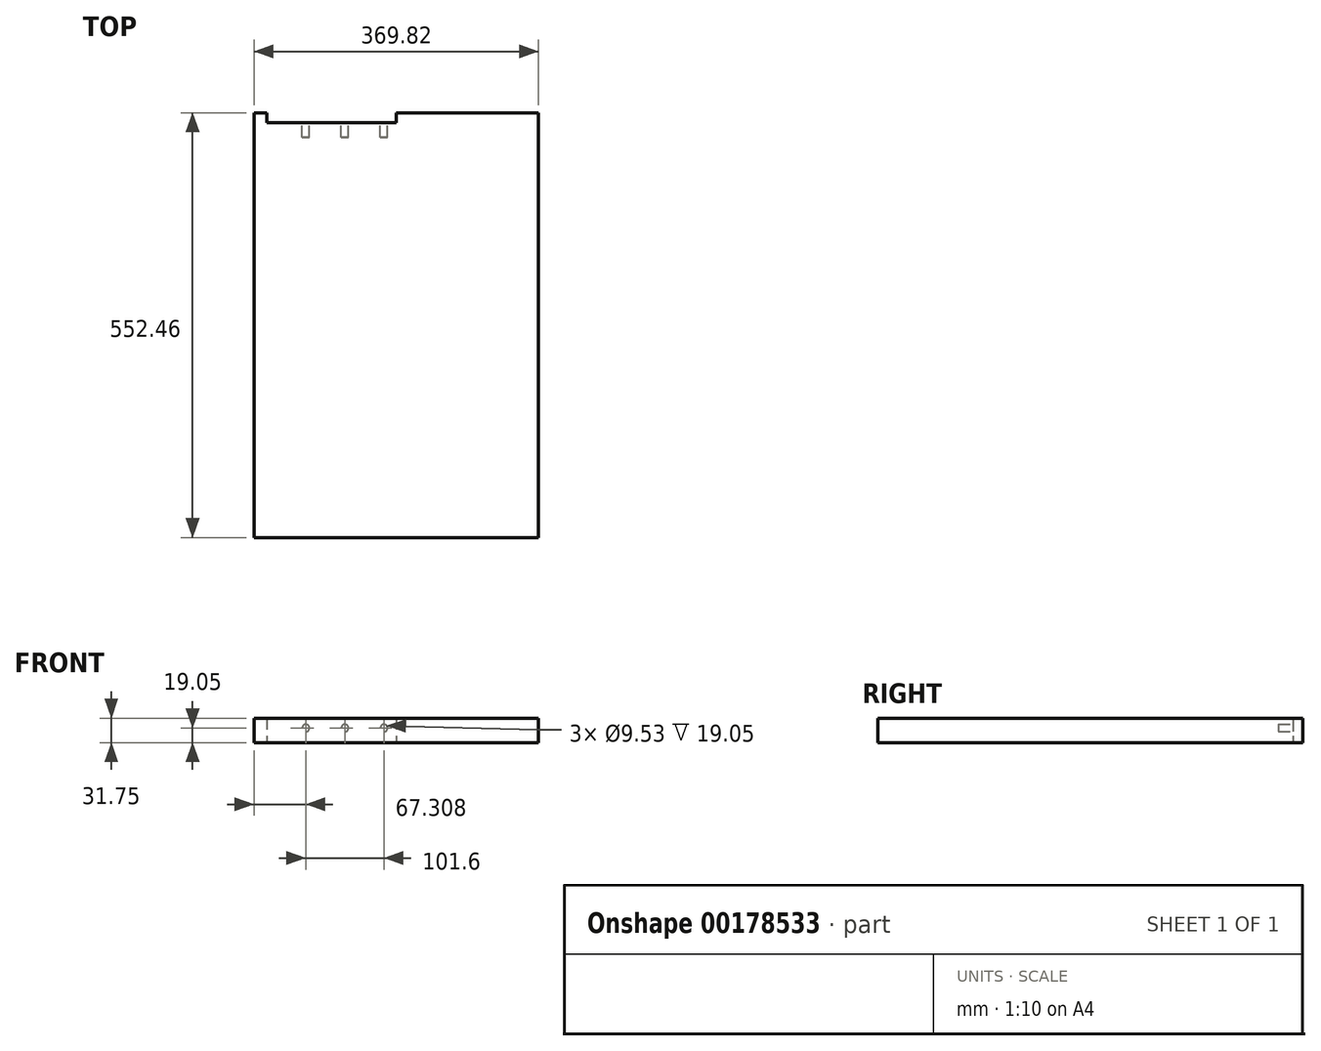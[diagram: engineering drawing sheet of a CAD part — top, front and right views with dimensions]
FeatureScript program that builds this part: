
annotation { "Feature Type Name" : "Feature", "Feature Type Description" : "" }
export const myFeature = defineFeature(function(context is Context, id is Id, definition is map)
    precondition{}
    {
        {
            var Q0;
            Q0=qCreatedBy(makeId("Top.planeOp"),FACE);
            var sketch = newSketch(context, id + "F0", { "sketchPlane" : qUnion([Q0])});
            skLineSegment(sketch, "E0.bottom", {"start": v(184.91, 276.23) * mm, "end": v(-0.13, 276.23) * mm});
            skLineSegment(sketch, "E0.top", {"start": v(184.91, -276.23) * mm, "end": v(-184.91, -276.23) * mm});
            skLineSegment(sketch, "E0.left", {"start": v(184.91, 276.23) * mm, "end": v(184.91, -276.23) * mm});
            skLineSegment(sketch, "E0.right", {"start": v(-184.91, 276.23) * mm, "end": v(-184.91, -276.23) * mm});
            skPoint(sketch, "E0.middle", {"position": v(0, 0) * mm});
            skLineSegment(sketch, "E1", {"start": v(-168.4, 276.23) * mm, "end": v(-168.4, 263.53) * mm});
            skLineSegment(sketch, "E2", {"start": v(-168.4, 263.53) * mm, "end": v(-0.13, 263.53) * mm});
            skLineSegment(sketch, "E3", {"start": v(-0.13, 263.53) * mm, "end": v(-0.13, 276.23) * mm});
            skLineSegment(sketch, "E4.trimOffspring", {"start": v(-168.4, 276.23) * mm, "end": v(-184.91, 276.23) * mm});
            skSolve(sketch);
        }
        {
            var Q0;
            Q0 = qSketchRegion(id + "F0", true);
            extrude(context, id + "F1", {"entities" : qUnion([Q0]), "depth" : 31.75 * mm});
        }
        {
            var Q0;
            Q0=makeQuery(id+"F1.opExtrude","SWEPT_FACE",FACE,{"disambiguationData":[OSD([sQuery(id+"F0.wireOp",EDGE,"E2")])]});
            var sketch = newSketch(context, id + "F2", { "sketchPlane" : qUnion([Q0])});
            skCircle(sketch, "E5", {"center": v(117.6, 19.05) * mm, "radius": 4.76 * mm});
            skCircle(sketch, "E6.1.0.0", {"center": v(66.8, 19.05) * mm, "radius": 4.76 * mm});
            skCircle(sketch, "E6.2.0.0", {"center": v(16, 19.05) * mm, "radius": 4.76 * mm});
            skLineSegment(sketch, "E6.direction1", {"start": v(117.6, 19.05) * mm, "end": v(66.8, 19.05) * mm, "construction": true});
            skSolve(sketch);
        }
        {
            var Q0;
            Q0 = qSketchRegion(id + "F2", true);
            extrude(context, id + "F3", {"entities" : qUnion([Q0]), "operationType" : NewBodyOperationType.REMOVE, "oppositeDirection" : true, "depth" : 19.05 * mm});
        }
    });
